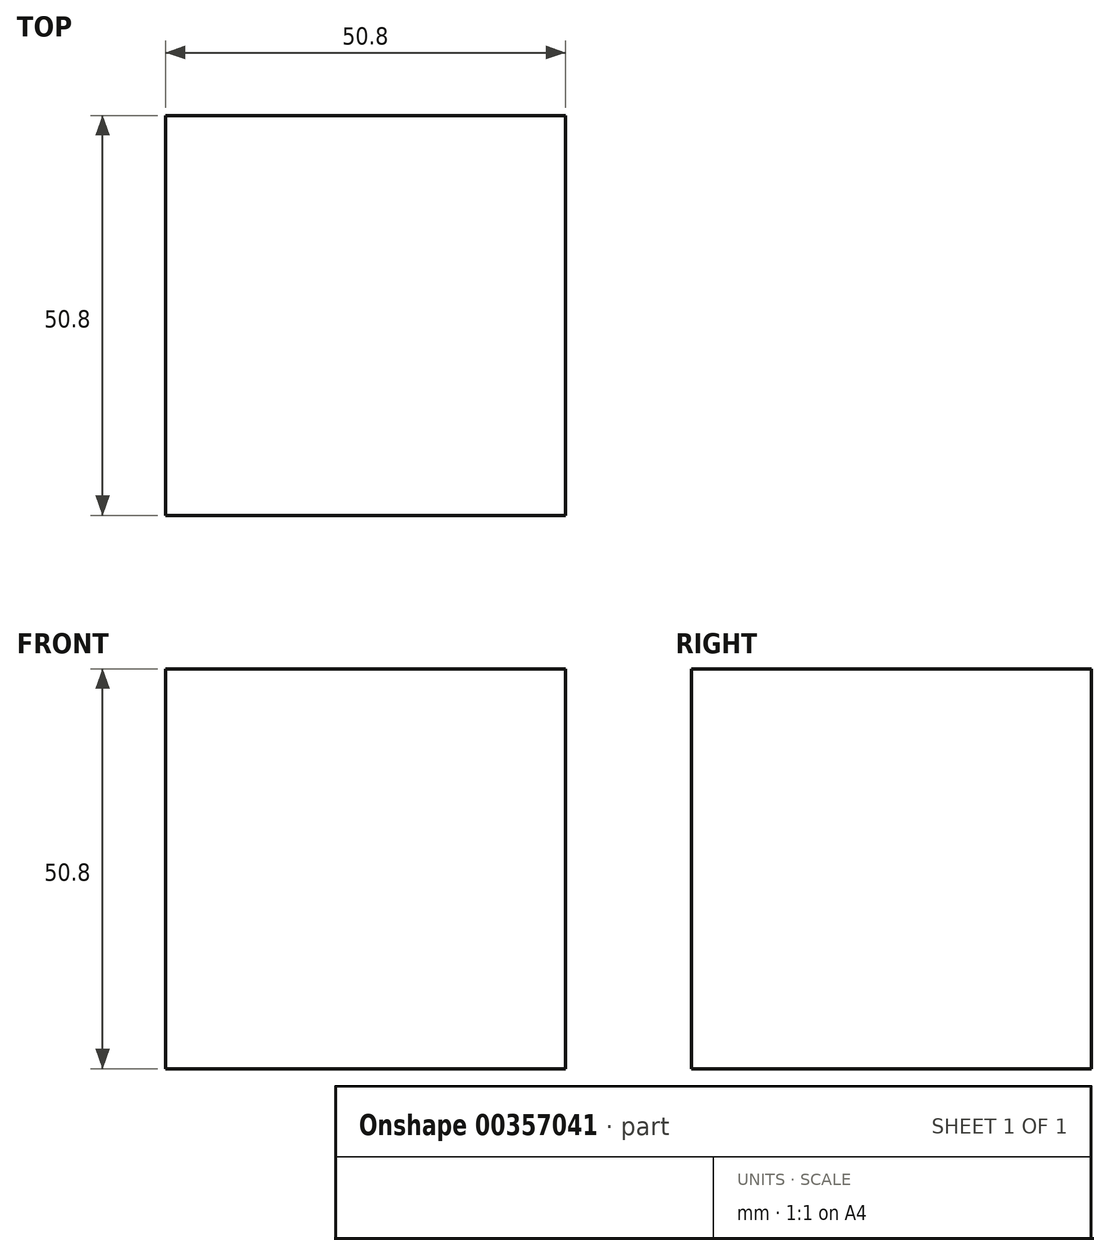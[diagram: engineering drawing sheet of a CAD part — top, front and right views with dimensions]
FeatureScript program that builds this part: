
annotation { "Feature Type Name" : "Feature", "Feature Type Description" : "" }
export const myFeature = defineFeature(function(context is Context, id is Id, definition is map)
    precondition{}
    {
        {
            var Q0;
            Q0=qCreatedBy(makeId("Front.planeOp"),FACE);
            var sketch = newSketch(context, id + "F0", { "sketchPlane" : qUnion([Q0])});
            skLineSegment(sketch, "E0", {"start": v(0, 0) * mm, "end": v(50.8, 0) * mm});
            skLineSegment(sketch, "E1", {"start": v(50.8, 50.8) * mm, "end": v(0, 50.8) * mm});
            skLineSegment(sketch, "E2", {"start": v(0, 50.8) * mm, "end": v(0, 0) * mm});
            skLineSegment(sketch, "E3", {"start": v(50.8, 0) * mm, "end": v(50.8, 50.8) * mm});
            skSolve(sketch);
        }
        {
            var Q0;
            Q0 = qSketchRegion(id + "F0", true);
            extrude(context, id + "F1", {"entities" : qUnion([Q0]), "depth" : 50.8 * mm});
        }
    });
